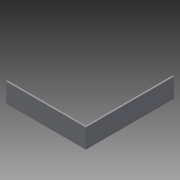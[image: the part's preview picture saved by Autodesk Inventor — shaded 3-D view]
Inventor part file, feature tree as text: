
AUTODESK INVENTOR PART (.ipt)
format: ipt  version: 2015 (Build 190159000, 159)  size: 131,072 bytes
history: native  units: in
note: dims shown in document units (in); Inventor stores cm internally (conversion verified against a paired STEP export)
features: extrude x2
ambient origin geometry x8: Origin, YZ Plane, XZ Plane, XY Plane, X Axis, Y Axis, Z Axis, Center Point
bodies: Body1 (feature_tree)
feature tree (2):
  extrude  "Extrusion4"  Depth=25.5906in
  extrude  "Extrusion5"  Depth=25.5906in
